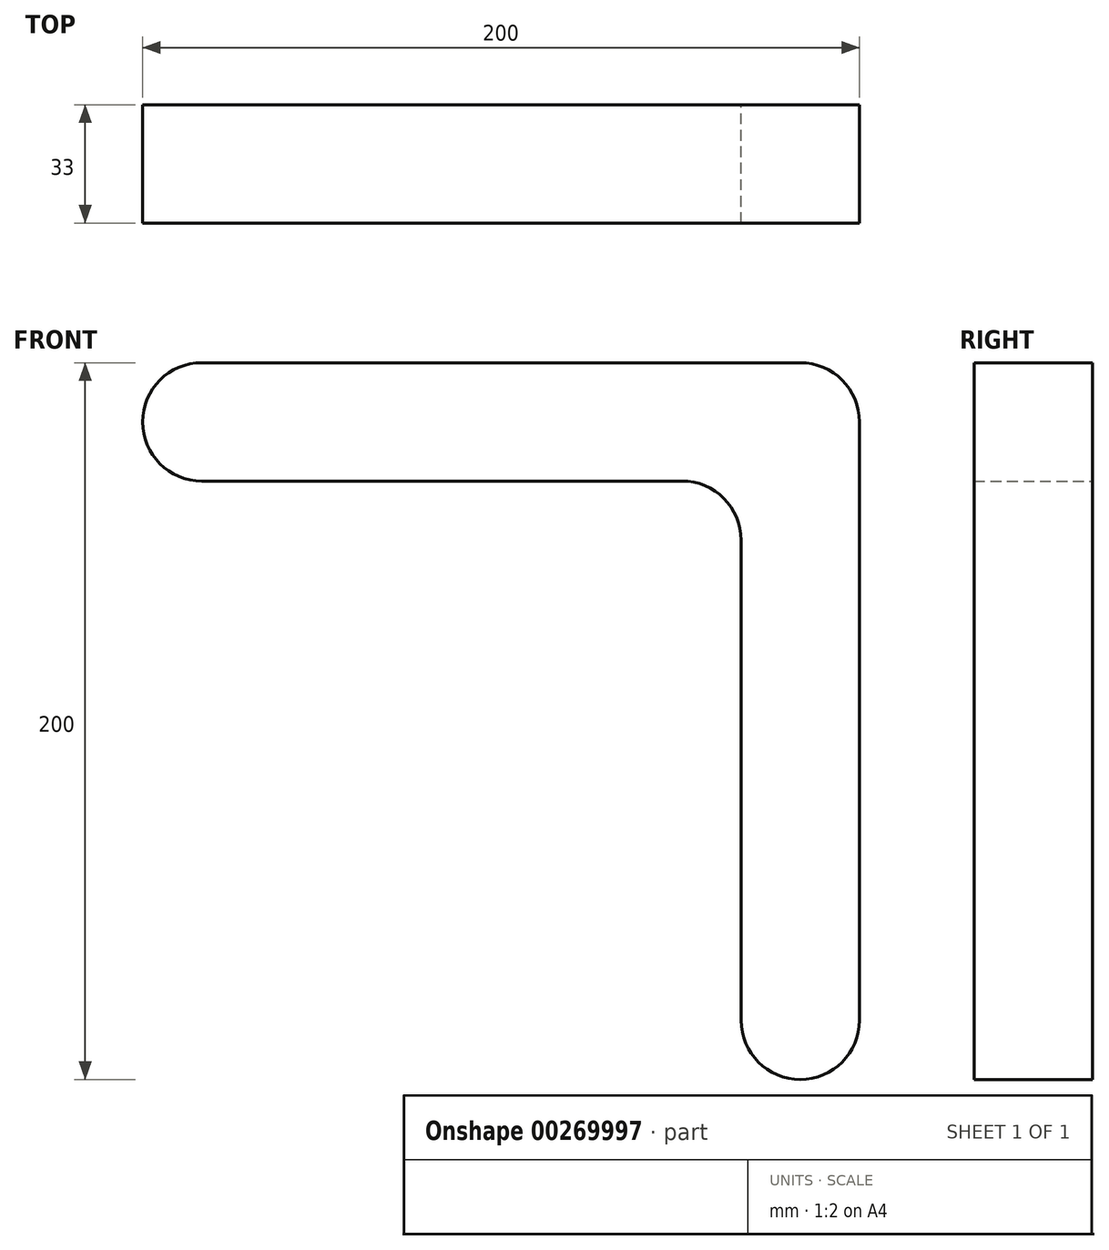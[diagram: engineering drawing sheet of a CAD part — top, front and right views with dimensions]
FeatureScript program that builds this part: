
annotation { "Feature Type Name" : "Feature", "Feature Type Description" : "" }
export const myFeature = defineFeature(function(context is Context, id is Id, definition is map)
    precondition{}
    {
        {
            var Q0;
            Q0=qCreatedBy(makeId("Front.planeOp"),FACE);
            var sketch = newSketch(context, id + "F0", { "sketchPlane" : qUnion([Q0])});
            skArc(sketch, "E0", {"start": v(0, 16.5) * mm, "mid": v(-16.5, 0) * mm, "end": v(0, -16.5) * mm});
            skArc(sketch, "E1", {"start": v(150.5, -167) * mm, "mid": v(167, -183.5) * mm, "end": v(183.5, -167) * mm});
            skLineSegment(sketch, "E2", {"start": v(0, 16.5) * mm, "end": v(167, 16.5) * mm});
            skLineSegment(sketch, "E3", {"start": v(183.5, -167) * mm, "end": v(183.5, 0) * mm});
            skLineSegment(sketch, "E4", {"start": v(0, -16.5) * mm, "end": v(134, -16.5) * mm});
            skLineSegment(sketch, "E5", {"start": v(150.5, -167) * mm, "end": v(150.5, -33) * mm});
            skPoint(sketch, "E6.visualSharp", {"position": v(183.5, 16.5) * mm});
            skArc(sketch, "E6.filletArc", {"start": v(183.5, 0) * mm, "mid": v(178.67, 11.67) * mm, "end": v(167, 16.5) * mm});
            skPoint(sketch, "E7.visualSharp", {"position": v(150.5, -16.5) * mm});
            skArc(sketch, "E7.filletArc", {"start": v(150.5, -33) * mm, "mid": v(145.67, -21.33) * mm, "end": v(134, -16.5) * mm});
            skSolve(sketch);
        }
        {
            var Q0;
            Q0=makeQuery(id+"F0.imprint","IMPRINT",FACE,{"disambiguationData":[TD([[makeQuery(id+"F0.imprint","IMPRINT",EDGE,{"derivedFrom":sQuery(id+"F0.wireOp",EDGE,"E0")}),1.0]])]});
            extrude(context, id + "F1", {"entities" : qUnion([Q0]), "endBound" : BoundingType.SYMMETRIC, "depth" : 33 * mm});
        }
    });
